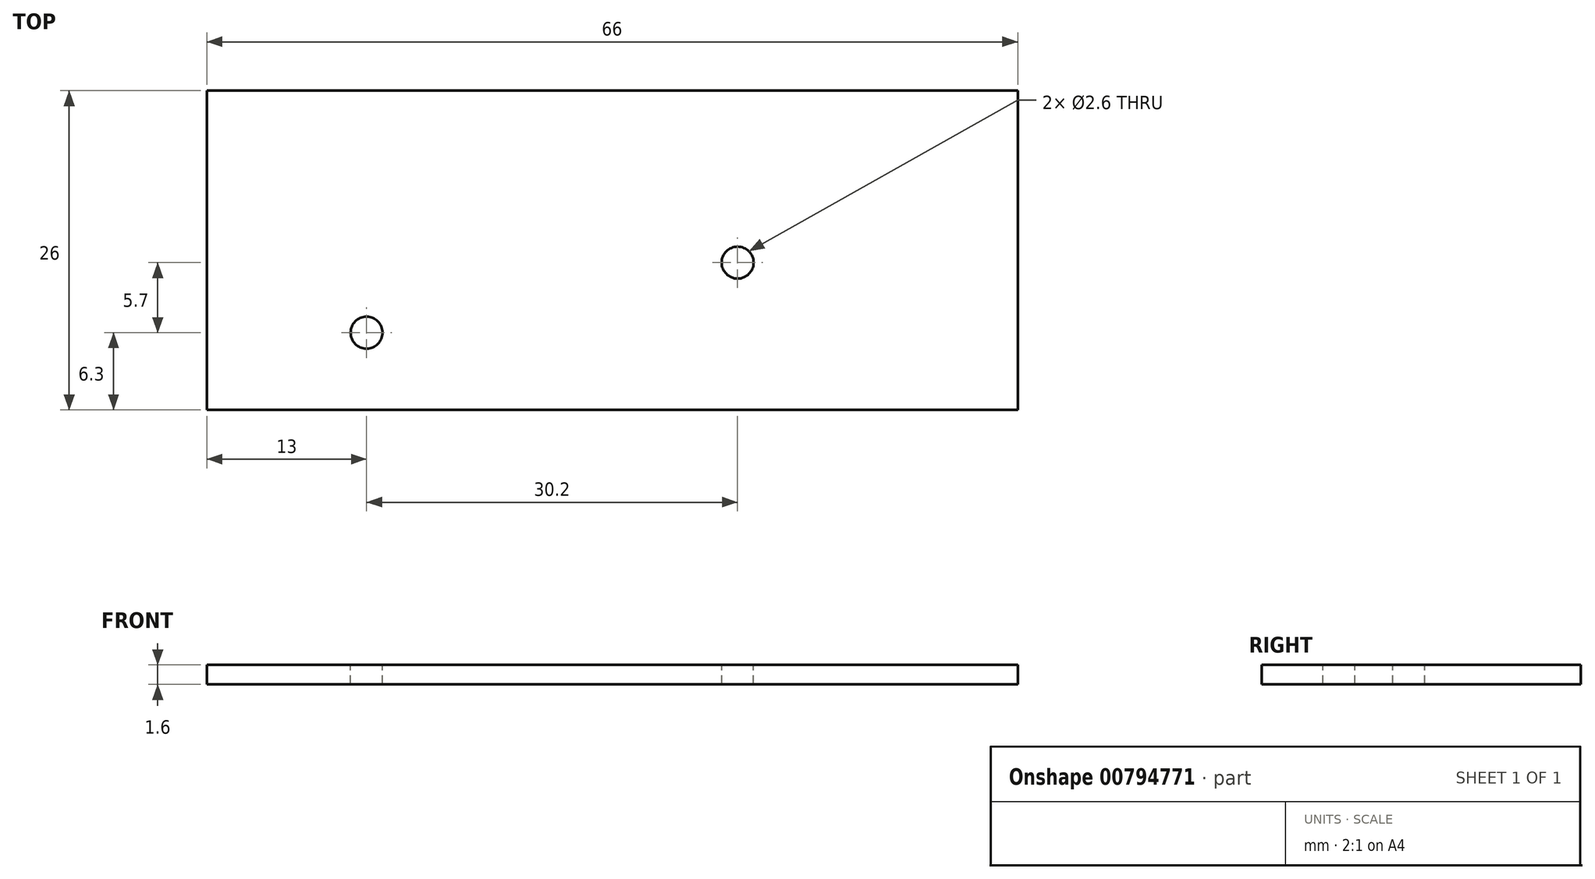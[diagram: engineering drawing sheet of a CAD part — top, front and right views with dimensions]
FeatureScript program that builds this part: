
annotation { "Feature Type Name" : "Feature", "Feature Type Description" : "" }
export const myFeature = defineFeature(function(context is Context, id is Id, definition is map)
    precondition{}
    {
        {
            var Q0;
            Q0=qCreatedBy(makeId("Top.planeOp"),FACE);
            var sketch = newSketch(context, id + "F0", { "sketchPlane" : qUnion([Q0])});
            skLineSegment(sketch, "E0.bottom", {"start": v(0, 0) * mm, "end": v(66, 0) * mm});
            skLineSegment(sketch, "E0.top", {"start": v(0, 26) * mm, "end": v(66, 26) * mm});
            skLineSegment(sketch, "E0.left", {"start": v(0, 0) * mm, "end": v(0, 26) * mm});
            skLineSegment(sketch, "E0.right", {"start": v(66, 0) * mm, "end": v(66, 26) * mm});
            skSolve(sketch);
        }
        {
            var Q0;
            Q0=makeQuery(id+"F0.imprint","IMPRINT",FACE,{"disambiguationData":[TD([[makeQuery(id+"F0.imprint","IMPRINT",EDGE,{"derivedFrom":sQuery(id+"F0.wireOp",EDGE,"E0.bottom")}),1.0]])]});
            extrude(context, id + "F1", {"entities" : qUnion([Q0]), "depth" : 1.6 * mm, "offsetDistance" : 25 * mm});
        }
        {
            var Q0;
            Q0=makeQuery(id+"F1.opExtrude","CAP_FACE",FACE,{"disambiguationData":[OSD([sQuery(id+"F0.wireOp",EDGE,"E0.bottom"),sQuery(id+"F0.wireOp",EDGE,"E0.top"),sQuery(id+"F0.wireOp",EDGE,"E0.left"),sQuery(id+"F0.wireOp",EDGE,"E0.right")])],"isStart":false});
            var sketch = newSketch(context, id + "F2", { "sketchPlane" : qUnion([Q0])});
            skLineSegment(sketch, "E1", {"start": v(-7, 5.5) * mm, "end": v(19.83, 5.5) * mm});
            skSolve(sketch);
        }
        {
            var Q0;
            Q0=makeQuery(id+"F2.imprint","IMPRINT",FACE,{"disambiguationData":[TD([[makeQuery(id+"F2.imprint","IMPRINT",EDGE,{"derivedFrom":makeQuery(id+"F1.opExtrude","CAP_EDGE",EDGE,{"disambiguationData":[OSD([sQuery(id+"F0.wireOp",EDGE,"E0.bottom")])],"isStart":false})}),1.0]])]});
            var sketch = newSketch(context, id + "F3", { "sketchPlane" : qUnion([Q0])});
            skCircle(sketch, "E2", {"center": v(13, 6.3) * mm, "radius": 1.3 * mm});
            skCircle(sketch, "E3", {"center": v(43.2, 12) * mm, "radius": 1.3 * mm});
            skSolve(sketch);
        }
        {
            var Q0;
            Q0=makeQuery(id+"F3.imprint","IMPRINT",FACE,{"disambiguationData":[TD([[makeQuery(id+"F3.imprint","IMPRINT",EDGE,{"derivedFrom":sQuery(id+"F3.wireOp",EDGE,"E2")}),1.0]])]});
            var Q1;
            Q1=makeQuery(id+"F3.imprint","IMPRINT",FACE,{"disambiguationData":[TD([[makeQuery(id+"F3.imprint","IMPRINT",EDGE,{"derivedFrom":sQuery(id+"F3.wireOp",EDGE,"E3")}),1.0]])]});
            extrude(context, id + "F4", {"entities" : qUnion([Q0, Q1]), "operationType" : NewBodyOperationType.REMOVE, "endBound" : BoundingType.UP_TO_NEXT, "oppositeDirection" : true, "depth" : 25 * mm, "offsetDistance" : 25 * mm});
        }
        {
            var Q0;
            Q0=makeQuery(id+"F2.imprint","IMPRINT",FACE,{"disambiguationData":[TD([[makeQuery(id+"F2.imprint","IMPRINT",EDGE,{"derivedFrom":makeQuery(id+"F1.opExtrude","CAP_EDGE",EDGE,{"disambiguationData":[OSD([sQuery(id+"F0.wireOp",EDGE,"E0.bottom")])],"isStart":false})}),1.0]])]});
            var sketch = newSketch(context, id + "F5", { "sketchPlane" : qUnion([Q0])});
            skLineSegment(sketch, "E4.bottom", {"start": v(52.6, 11.33) * mm, "end": v(65.8, 11.33) * mm});
            skLineSegment(sketch, "E4.top", {"start": v(52.6, 1.7) * mm, "end": v(65.8, 1.7) * mm});
            skLineSegment(sketch, "E4.left", {"start": v(52.6, 11.33) * mm, "end": v(52.6, 1.7) * mm});
            skLineSegment(sketch, "E4.right", {"start": v(65.8, 11.33) * mm, "end": v(65.8, 1.7) * mm});
            skLineSegment(sketch, "E5.bottom", {"start": v(49.05, 24.1) * mm, "end": v(65.8, 24.1) * mm});
            skLineSegment(sketch, "E5.top", {"start": v(49.05, 14.78) * mm, "end": v(65.8, 14.78) * mm});
            skLineSegment(sketch, "E5.left", {"start": v(49.05, 24.1) * mm, "end": v(49.05, 14.78) * mm});
            skLineSegment(sketch, "E5.right", {"start": v(65.8, 24.1) * mm, "end": v(65.8, 14.78) * mm});
            skSolve(sketch);
        }
    });
